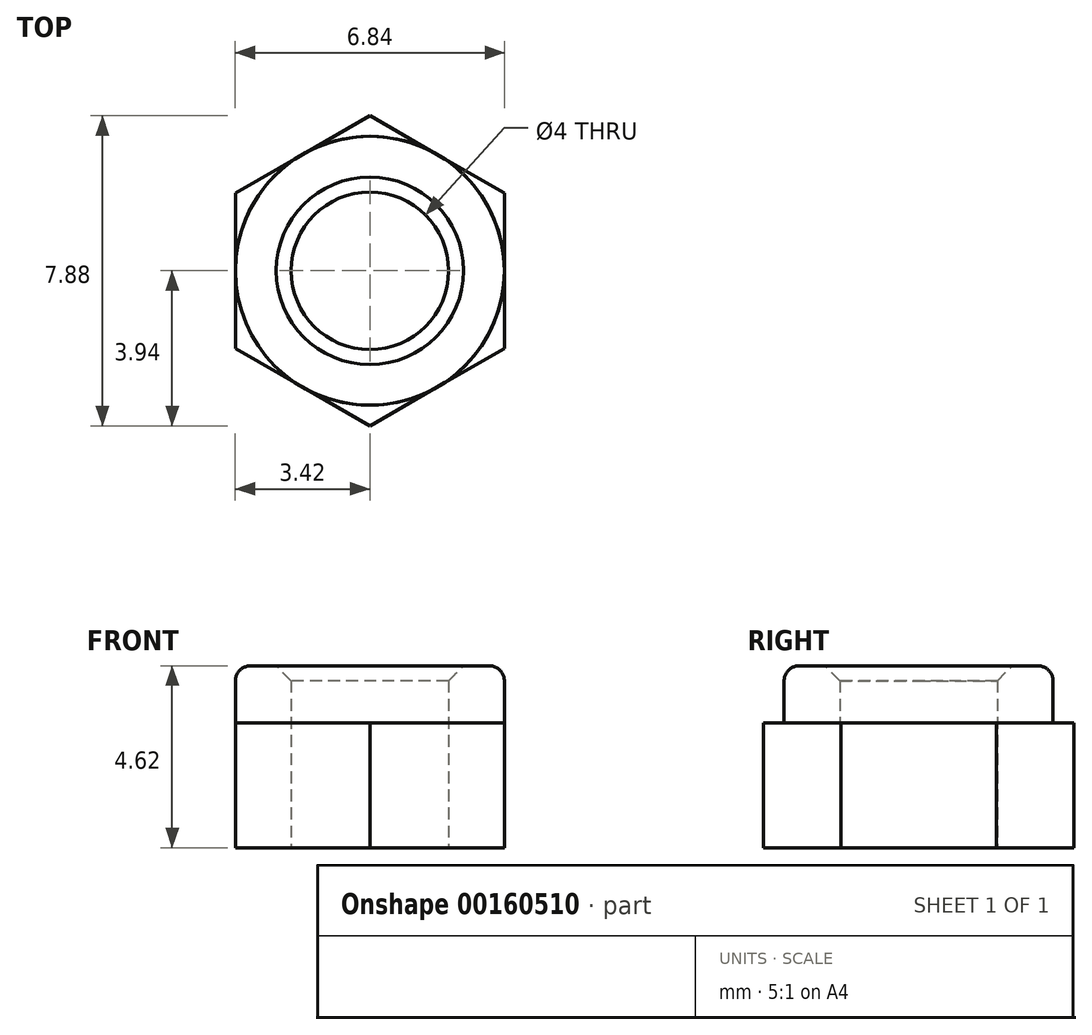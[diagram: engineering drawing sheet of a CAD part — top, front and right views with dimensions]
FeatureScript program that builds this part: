
annotation { "Feature Type Name" : "Feature", "Feature Type Description" : "" }
export const myFeature = defineFeature(function(context is Context, id is Id, definition is map)
    precondition{}
    {
        {
            var Q0;
            Q0=qCreatedBy(makeId("Top.planeOp"),FACE);
            var sketch = newSketch(context, id + "F0", { "sketchPlane" : qUnion([Q0])});
            skCircle(sketch, "E0.cCircle", {"center": v(0, 0) * mm, "radius": 3.42 * mm, "construction": true});
            skLineSegment(sketch, "E0.0", {"start": v(3.42, 1.97) * mm, "end": v(3.42, -1.97) * mm});
            skLineSegment(sketch, "E0.1", {"start": v(3.42, -1.97) * mm, "end": v(0, -3.94) * mm});
            skLineSegment(sketch, "E0.2", {"start": v(0, -3.94) * mm, "end": v(-3.42, -1.97) * mm});
            skLineSegment(sketch, "E0.3", {"start": v(-3.42, -1.97) * mm, "end": v(-3.42, 1.97) * mm});
            skLineSegment(sketch, "E0.4", {"start": v(-3.42, 1.97) * mm, "end": v(0, 3.94) * mm});
            skLineSegment(sketch, "E0.5", {"start": v(0, 3.94) * mm, "end": v(3.42, 1.97) * mm});
            skPoint(sketch, "E0.0.midPoint", {"position": v(3.42, 0) * mm});
            skCircle(sketch, "E1", {"center": v(0, 0) * mm, "radius": 2 * mm});
            skSolve(sketch);
        }
        {
            var Q0;
            Q0=qSketchRegion(id+"F0",true);
            extrude(context, id + "F1", {"entities" : qUnion([Q0]), "depth" : 3.17 * mm});
        }
        {
            var Q0;
            Q0=makeQuery(id+"F1.opExtrude","CAP_FACE",FACE,{"disambiguationData":[OSD([sQuery(id+"F0.wireOp",EDGE,"E0.0"),sQuery(id+"F0.wireOp",EDGE,"E0.1"),sQuery(id+"F0.wireOp",EDGE,"E0.2"),sQuery(id+"F0.wireOp",EDGE,"E0.3"),sQuery(id+"F0.wireOp",EDGE,"E0.4"),sQuery(id+"F0.wireOp",EDGE,"E0.5"),sQuery(id+"F0.wireOp",EDGE,"E1")])],"isStart":false});
            var sketch = newSketch(context, id + "F2", { "sketchPlane" : qUnion([Q0])});
            skCircle(sketch, "E2", {"center": v(0, 0) * mm, "radius": 3.42 * mm});
            skCircle(sketch, "E3", {"center": v(0, 0) * mm, "radius": 2 * mm});
            skSolve(sketch);
        }
        {
            var Q0;
            Q0=qSketchRegion(id+"F2",true);
            extrude(context, id + "F3", {"entities" : qUnion([Q0]), "operationType" : NewBodyOperationType.ADD, "depth" : 1.45 * mm});
        }
        {
            var Q0;
            Q0=makeQuery(id+"F3.opExtrude","CAP_EDGE",EDGE,{"disambiguationData":[OSD([sQuery(id+"F2.wireOp",EDGE,"E2")])],"isStart":false});
            fillet(context, id + "F4", {"entities" : qUnion([Q0]), "radius" : 0.38 * mm, "tangentPropagation" : true, "allowEdgeOverflow" : false});
        }
        {
            var Q0;
            Q0=makeQuery(id+"F3.opExtrude","CAP_EDGE",EDGE,{"disambiguationData":[OSD([sQuery(id+"F2.wireOp",EDGE,"E3")])],"isStart":false});
            chamfer(context, id + "F5", {"entities" : qUnion([Q0]), "width" : 0.38 * mm, "tangentPropagation" : true});
        }
    });
